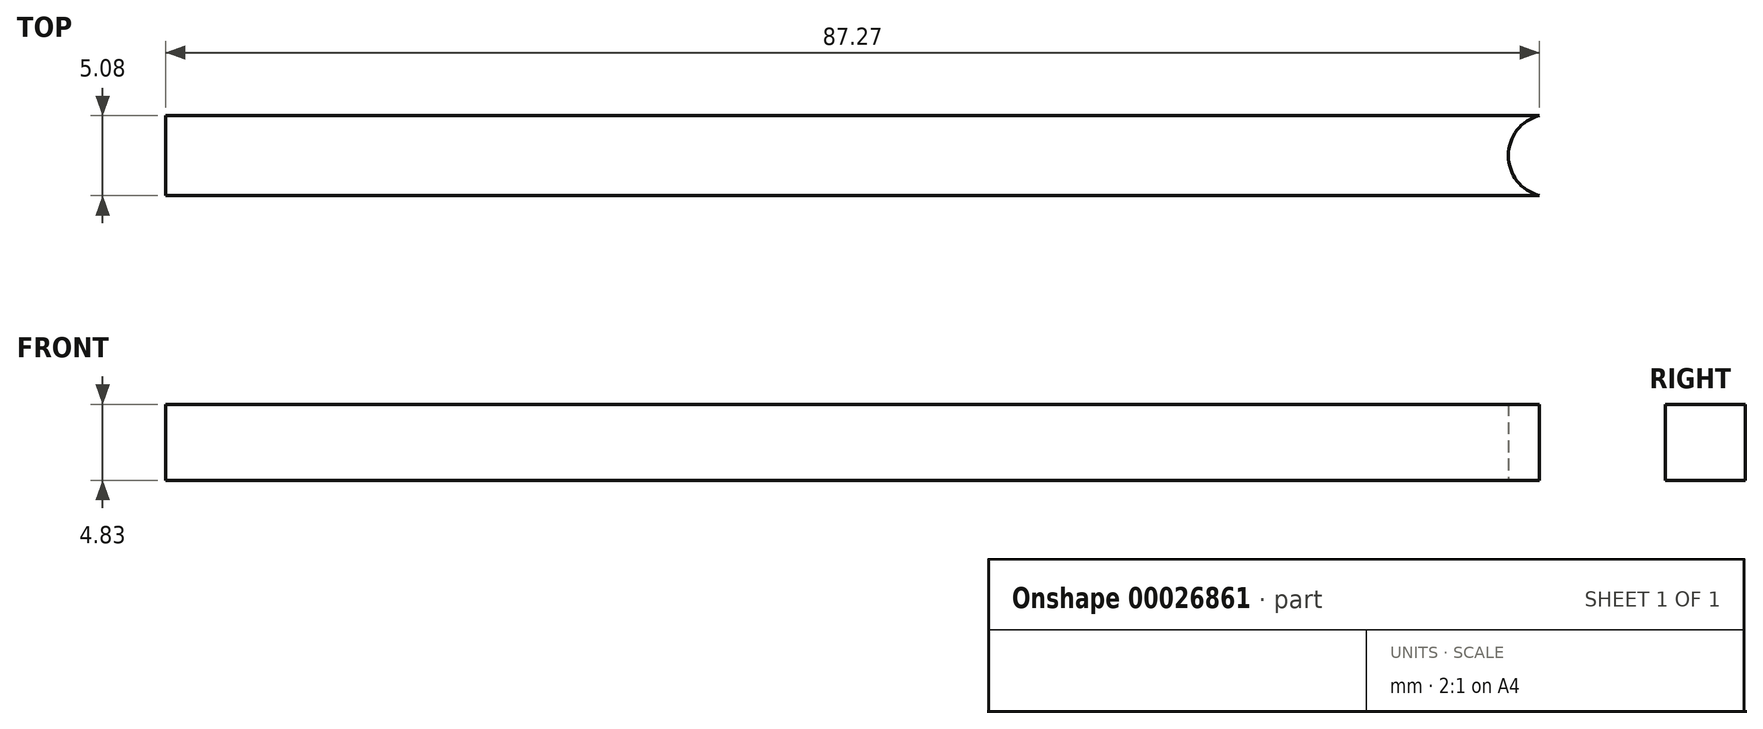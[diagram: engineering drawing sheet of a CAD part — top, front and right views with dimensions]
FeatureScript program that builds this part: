
annotation { "Feature Type Name" : "Feature", "Feature Type Description" : "" }
export const myFeature = defineFeature(function(context is Context, id is Id, definition is map)
    precondition{}
    {
        {
            var Q0;
            Q0=qCreatedBy(makeId("Top.planeOp"),FACE);
            var sketch = newSketch(context, id + "F0", { "sketchPlane" : qUnion([Q0])});
            skLineSegment(sketch, "E0.bottom", {"start": v(-78.06, 18.8) * mm, "end": v(9.85, 18.8) * mm});
            skLineSegment(sketch, "E0.top", {"start": v(-78.06, 13.71) * mm, "end": v(9.85, 13.71) * mm});
            skLineSegment(sketch, "E0.left", {"start": v(-78.06, 18.8) * mm, "end": v(-78.06, 13.71) * mm});
            skPoint(sketch, "E1.center.orphan", {"position": v(9.85, 16.25) * mm});
            skArc(sketch, "E2", {"start": v(9.2, 18.8) * mm, "mid": v(7.23, 16.25) * mm, "end": v(9.2, 13.71) * mm});
            skSolve(sketch);
        }
        {
            var Q0;
            {var subQ1=sQuery(id+"F0.wireOp",EDGE,"E0.left");Q0=makeQuery(id+"F0.imprint","IMPRINT",FACE,{"disambiguationData":[TD([[makeQuery(id+"F0.imprint","IMPRINT",EDGE,{"derivedFrom":subQ1}),1.0]])]});}
            extrude(context, id + "F1", {"entities" : qUnion([Q0]), "depth" : 4.83 * mm});
        }
    });
